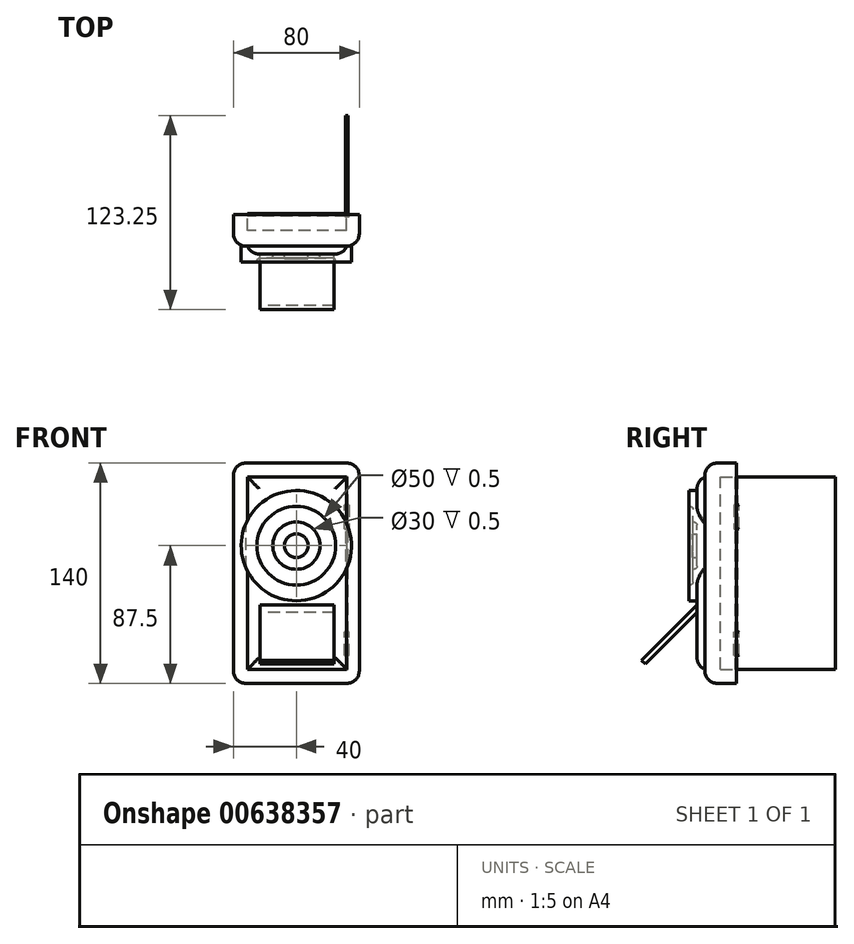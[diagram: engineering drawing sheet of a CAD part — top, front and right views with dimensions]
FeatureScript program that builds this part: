
annotation { "Feature Type Name" : "Feature", "Feature Type Description" : "" }
export const myFeature = defineFeature(function(context is Context, id is Id, definition is map)
    precondition{}
    {
        {
            var Q0;
            Q0=qCreatedBy(makeId("Front.planeOp"),FACE);
            var sketch = newSketch(context, id + "F0", { "sketchPlane" : qUnion([Q0])});
            skLineSegment(sketch, "E0", {"start": v(0, 0) * mm, "end": v(0, 140) * mm});
            skLineSegment(sketch, "E1", {"start": v(0, 140) * mm, "end": v(80, 140) * mm});
            skLineSegment(sketch, "E2", {"start": v(80, 140) * mm, "end": v(80, 0) * mm});
            skLineSegment(sketch, "E3", {"start": v(80, 0) * mm, "end": v(0, 0) * mm});
            skLineSegment(sketch, "E4", {"start": v(0, 0) * mm, "end": v(9, 0) * mm});
            skLineSegment(sketch, "E5", {"start": v(9, 0) * mm, "end": v(9, 131) * mm});
            skLineSegment(sketch, "E6", {"start": v(9, 131) * mm, "end": v(72, 131) * mm});
            skLineSegment(sketch, "E7", {"start": v(72, 131) * mm, "end": v(72, 9) * mm});
            skLineSegment(sketch, "E8", {"start": v(72, 9) * mm, "end": v(9, 9) * mm});
            skSolve(sketch);
        }
        {
            var Q0;
            Q0=makeQuery(id+"F0.imprint","IMPRINT",FACE,{"disambiguationData":[TD([[makeQuery(id+"F0.imprint","IMPRINT",EDGE,{"derivedFrom":sQuery(id+"F0.wireOp",EDGE,"E0")}),-1.0]])]});
            extrude(context, id + "F1", {"entities" : qUnion([Q0]), "depth" : 20 * mm, "offsetDistance" : 25 * mm});
        }
        {
            var Q0;
            {var subQ0=sQuery(id+"F0.wireOp",EDGE,"E6");Q0=makeQuery(id+"F0.imprint","IMPRINT",FACE,{"disambiguationData":[TD([[makeQuery(id+"F0.imprint","IMPRINT",EDGE,{"derivedFrom":subQ0}),-1.0]])]});}
            extrude(context, id + "F2", {"entities" : qUnion([Q0]), "operationType" : NewBodyOperationType.ADD, "depth" : 25 * mm, "offsetDistance" : 25 * mm});
        }
        {
            var Q0;
            {var subQ0=sQuery(id+"F0.wireOp",EDGE,"E6");Q0=makeQuery(id+"F0.imprint","IMPRINT",FACE,{"disambiguationData":[TD([[makeQuery(id+"F0.imprint","IMPRINT",EDGE,{"derivedFrom":subQ0}),-1.0]])]});}
            extrude(context, id + "F3", {"entities" : qUnion([Q0]), "operationType" : NewBodyOperationType.REMOVE, "depth" : 10 * mm, "offsetDistance" : 25 * mm});
        }
        {
            var Q0;
            Q0=makeQuery(id+"F1.opExtrude","SWEPT_EDGE",EDGE,{"disambiguationData":[OSD([sQuery(id+"F0.wireOp",EDGE,"E0"),sQuery(id+"F0.wireOp",EDGE,"E4")])]});
            var Q1;
            Q1=makeQuery(id+"F1.opExtrude","SWEPT_EDGE",EDGE,{"disambiguationData":[OSD([sQuery(id+"F0.wireOp",EDGE,"E2"),sQuery(id+"F0.wireOp",EDGE,"E3")])]});
            var Q2;
            Q2=makeQuery(id+"F1.opExtrude","SWEPT_EDGE",EDGE,{"disambiguationData":[OSD([sQuery(id+"F0.wireOp",EDGE,"E0"),sQuery(id+"F0.wireOp",EDGE,"E1")])]});
            var Q3;
            Q3=makeQuery(id+"F1.opExtrude","SWEPT_EDGE",EDGE,{"disambiguationData":[OSD([sQuery(id+"F0.wireOp",EDGE,"E1"),sQuery(id+"F0.wireOp",EDGE,"E2")])]});
            var Q4;
            Q4=makeQuery(id+"F1.opExtrude","CAP_EDGE",EDGE,{"disambiguationData":[OSD([sQuery(id+"F0.wireOp",EDGE,"E1")])],"isStart":false});
            var Q5;
            Q5=makeQuery(id+"F1.opExtrude","CAP_EDGE",EDGE,{"disambiguationData":[OSD([sQuery(id+"F0.wireOp",EDGE,"E0")])],"isStart":false});
            var Q6;
            Q6=makeQuery(id+"F1.opExtrude","CAP_EDGE",EDGE,{"disambiguationData":[OSD([sQuery(id+"F0.wireOp",EDGE,"E2")])],"isStart":false});
            var Q7;
            Q7=makeQuery(id+"F1.opExtrude","CAP_EDGE",EDGE,{"disambiguationData":[OSD([sQuery(id+"F0.wireOp",EDGE,"E3"),sQuery(id+"F0.wireOp",EDGE,"E4")])],"isStart":false});
            var Q8;
            Q8=makeQuery(id+"F2.opExtrude","CAP_EDGE",EDGE,{"disambiguationData":[OSD([sQuery(id+"F0.wireOp",EDGE,"E7")])],"isStart":false});
            var Q9;
            Q9=makeQuery(id+"F2.opExtrude","CAP_EDGE",EDGE,{"disambiguationData":[OSD([sQuery(id+"F0.wireOp",EDGE,"E6")])],"isStart":false});
            var Q10;
            Q10=makeQuery(id+"F2.opExtrude","CAP_EDGE",EDGE,{"disambiguationData":[OSD([sQuery(id+"F0.wireOp",EDGE,"E5")])],"isStart":false});
            var Q11;
            Q11=makeQuery(id+"F2.opExtrude","CAP_EDGE",EDGE,{"disambiguationData":[OSD([sQuery(id+"F0.wireOp",EDGE,"E8")])],"isStart":false});
            fillet(context, id + "F4", {"entities" : qUnion([Q0, Q1, Q2, Q3, Q4, Q5, Q6, Q7, Q8, Q9, Q10, Q11]), "radius" : 8 * mm, "tangentPropagation" : true, "allowEdgeOverflow" : false});
        }
        {
            var Q0;
            Q0=makeQuery(id+"F0.imprint","IMPRINT",FACE,{"disambiguationData":[TD([[makeQuery(id+"F0.imprint","IMPRINT",EDGE,{"derivedFrom":sQuery(id+"F0.wireOp",EDGE,"E0")}),-1.0]])]});
            var sketch = newSketch(context, id + "F5", { "sketchPlane" : qUnion([Q0])});
            skLineSegment(sketch, "E9", {"start": v(0, 0) * mm, "end": v(72, 0) * mm});
            skLineSegment(sketch, "E10", {"start": v(72, 0) * mm, "end": v(72, 131) * mm});
            skLineSegment(sketch, "E11", {"start": v(72, 131) * mm, "end": v(72, 65.5) * mm});
            skLineSegment(sketch, "E12", {"start": v(72, 65.5) * mm, "end": v(72, 98.25) * mm});
            skLineSegment(sketch, "E13", {"start": v(72, 98.25) * mm, "end": v(70.5, 98.25) * mm});
            skLineSegment(sketch, "E14", {"start": v(70.5, 98.25) * mm, "end": v(70.5, 113.25) * mm});
            skLineSegment(sketch, "E15", {"start": v(70.5, 113.25) * mm, "end": v(73.5, 113.25) * mm});
            skLineSegment(sketch, "E16", {"start": v(73.5, 113.25) * mm, "end": v(73.5, 98.25) * mm});
            skLineSegment(sketch, "E17", {"start": v(73.5, 98.25) * mm, "end": v(72, 98.25) * mm});
            skLineSegment(sketch, "E18.MirrorCS", {"start": v(73.5, 32.75) * mm, "end": v(72, 32.75) * mm});
            skLineSegment(sketch, "E19.MirrorCS", {"start": v(72, 32.75) * mm, "end": v(70.5, 32.75) * mm});
            skLineSegment(sketch, "E20.MirrorCS", {"start": v(70.5, 32.75) * mm, "end": v(70.5, 17.75) * mm});
            skLineSegment(sketch, "E21.MirrorCS", {"start": v(73.5, 17.75) * mm, "end": v(73.5, 32.75) * mm});
            skLineSegment(sketch, "E22.MirrorCS", {"start": v(70.5, 17.75) * mm, "end": v(73.5, 17.75) * mm});
            skSolve(sketch);
        }
        {
            var Q0;
            {var subQ4=sQuery(id+"F5.wireOp",EDGE,"E16");Q0=makeQuery(id+"F5.imprint","IMPRINT",FACE,{"disambiguationData":[TD([[makeQuery(id+"F5.imprint","IMPRINT",EDGE,{"derivedFrom":subQ4}),-1.0]])]});}
            var Q1;
            {var subQ0=sQuery(id+"F5.wireOp",EDGE,"E13");Q1=makeQuery(id+"F5.imprint","IMPRINT",FACE,{"disambiguationData":[TD([[makeQuery(id+"F5.imprint","IMPRINT",EDGE,{"derivedFrom":subQ0}),-1.0]])]});}
            var Q2;
            {var subQ0=sQuery(id+"F5.wireOp",EDGE,"E18.MirrorCS");Q2=makeQuery(id+"F5.imprint","IMPRINT",FACE,{"disambiguationData":[TD([[makeQuery(id+"F5.imprint","IMPRINT",EDGE,{"derivedFrom":subQ0}),1.0]])]});}
            var Q3;
            {var subQ0=sQuery(id+"F5.wireOp",EDGE,"E19.MirrorCS");Q3=makeQuery(id+"F5.imprint","IMPRINT",FACE,{"disambiguationData":[TD([[makeQuery(id+"F5.imprint","IMPRINT",EDGE,{"derivedFrom":subQ0}),1.0]])]});}
            extrude(context, id + "F6", {"entities" : qUnion([Q0, Q1, Q2, Q3]), "endBound" : BoundingType.SYMMETRIC, "depth" : 3 * mm, "offsetDistance" : 25 * mm});
        }
        {
            var Q0;
            Q0=makeQuery(id+"F6.opExtrude","CAP_EDGE",EDGE,{"disambiguationData":[OSD([sQuery(id+"F5.wireOp",EDGE,"E16")])],"isStart":true});
            var Q1;
            Q1=makeQuery(id+"F6.opExtrude","CAP_EDGE",EDGE,{"disambiguationData":[OSD([sQuery(id+"F5.wireOp",EDGE,"E14")])],"isStart":true});
            var Q2;
            Q2=makeQuery(id+"F6.opExtrude","CAP_EDGE",EDGE,{"disambiguationData":[OSD([sQuery(id+"F5.wireOp",EDGE,"E14")])],"isStart":false});
            var Q3;
            Q3=makeQuery(id+"F6.opExtrude","CAP_EDGE",EDGE,{"disambiguationData":[OSD([sQuery(id+"F5.wireOp",EDGE,"E21.MirrorCS")])],"isStart":true});
            var Q4;
            Q4=makeQuery(id+"F6.opExtrude","CAP_EDGE",EDGE,{"disambiguationData":[OSD([sQuery(id+"F5.wireOp",EDGE,"E20.MirrorCS")])],"isStart":true});
            var Q5;
            Q5=makeQuery(id+"F6.opExtrude","CAP_EDGE",EDGE,{"disambiguationData":[OSD([sQuery(id+"F5.wireOp",EDGE,"E20.MirrorCS")])],"isStart":false});
            fillet(context, id + "F7", {"entities" : qUnion([Q0, Q1, Q2, Q3, Q4, Q5]), "radius" : 1.5 * mm, "tangentPropagation" : true, "allowEdgeOverflow" : false});
        }
        {
            var Q0;
            Q0=qCreatedBy(makeId("Front.planeOp"),FACE);
            var sketch = newSketch(context, id + "F8", { "sketchPlane" : qUnion([Q0])});
            skLineSegment(sketch, "E23", {"start": v(0, 0) * mm, "end": v(72, 0) * mm});
            skLineSegment(sketch, "E24", {"start": v(72, 0) * mm, "end": v(72, 9) * mm});
            skLineSegment(sketch, "E25", {"start": v(72, 9) * mm, "end": v(72, 131) * mm});
            skLineSegment(sketch, "E26", {"start": v(72, 131) * mm, "end": v(72.75, 131) * mm});
            skLineSegment(sketch, "E27", {"start": v(72.75, 131) * mm, "end": v(72, 131) * mm});
            skLineSegment(sketch, "E28", {"start": v(72, 131) * mm, "end": v(71.25, 131) * mm});
            skLineSegment(sketch, "E29", {"start": v(71.25, 131) * mm, "end": v(71.25, 9) * mm});
            skLineSegment(sketch, "E30", {"start": v(71.25, 9) * mm, "end": v(72.75, 9) * mm});
            skLineSegment(sketch, "E31", {"start": v(72.75, 9) * mm, "end": v(72.75, 131) * mm});
            skSolve(sketch);
        }
        {
            var Q0;
            {var subQ0=sQuery(id+"F8.wireOp",EDGE,"E25");Q0=makeQuery(id+"F8.imprint","IMPRINT",FACE,{"disambiguationData":[TD([[makeQuery(id+"F8.imprint","IMPRINT",EDGE,{"derivedFrom":subQ0}),1.0]])]});}
            var Q1;
            {var subQ0=sQuery(id+"F8.wireOp",EDGE,"E25");Q1=makeQuery(id+"F8.imprint","IMPRINT",FACE,{"disambiguationData":[TD([[makeQuery(id+"F8.imprint","IMPRINT",EDGE,{"derivedFrom":subQ0}),-1.0]])]});}
            extrude(context, id + "F9", {"entities" : qUnion([Q0, Q1]), "oppositeDirection" : true, "depth" : 63 * mm, "offsetDistance" : 25 * mm});
        }
        {
            var Q0;
            Q0=qCreatedBy(makeId("Front.planeOp"),FACE);
            var sketch = newSketch(context, id + "F10", { "sketchPlane" : qUnion([Q0])});
            skLineSegment(sketch, "E32", {"start": v(0, 0) * mm, "end": v(72, 0) * mm});
            skLineSegment(sketch, "E33", {"start": v(72, 0) * mm, "end": v(72, 9) * mm});
            skLineSegment(sketch, "E34", {"start": v(72, 9) * mm, "end": v(9, 9) * mm});
            skLineSegment(sketch, "E35", {"start": v(9, 9) * mm, "end": v(9, 131) * mm});
            skLineSegment(sketch, "E36", {"start": v(9, 131) * mm, "end": v(72, 131) * mm});
            skLineSegment(sketch, "E37", {"start": v(72, 131) * mm, "end": v(72, 9) * mm});
            skSolve(sketch);
        }
        {
            var Q0;
            Q0=makeQuery(id+"F10.imprint","IMPRINT",FACE,{"disambiguationData":[TD([[makeQuery(id+"F10.imprint","IMPRINT",EDGE,{"derivedFrom":sQuery(id+"F10.wireOp",EDGE,"E34")}),-1.0]])]});
            extrude(context, id + "F11", {"entities" : qUnion([Q0]), "endBound" : BoundingType.SYMMETRIC, "depth" : 1.5 * mm, "offsetDistance" : 25 * mm});
        }
        {
            var Q0;
            Q0=qCreatedBy(makeId("Right.planeOp"),FACE);
            var sketch = newSketch(context, id + "F12", { "sketchPlane" : qUnion([Q0])});
            skLineSegment(sketch, "E38", {"start": v(0, 0) * mm, "end": v(-25, 0) * mm});
            skLineSegment(sketch, "E39", {"start": v(-25, 0) * mm, "end": v(-25, 50) * mm});
            skLineSegment(sketch, "E40", {"start": v(-50, 25) * mm, "end": v(-60.25, 14.75) * mm});
            skLineSegment(sketch, "E41", {"start": v(-50, 25) * mm, "end": v(-25, 50) * mm});
            skLineSegment(sketch, "E42", {"start": v(-60.25, 14.75) * mm, "end": v(-57.78, 12.27) * mm});
            skLineSegment(sketch, "E43", {"start": v(-57.78, 12.27) * mm, "end": v(-25, 45.05) * mm});
            skLineSegment(sketch, "E44", {"start": v(-25, 45.05) * mm, "end": v(-25, 50) * mm});
            skSolve(sketch);
        }
        {
            var Q0;
            Q0=makeQuery(id+"F12.imprint","IMPRINT",FACE,{"disambiguationData":[TD([[makeQuery(id+"F12.imprint","IMPRINT",EDGE,{"derivedFrom":sQuery(id+"F12.wireOp",EDGE,"E40")}),1.0]])]});
            extrude(context, id + "F13", {"entities" : qUnion([Q0]), "operationType" : NewBodyOperationType.ADD, "depth" : 64 * mm, "offsetDistance" : 25 * mm});
        }
        {
            var Q0;
            Q0=makeQuery(id+"F13.opExtrude","CAP_FACE",FACE,{"disambiguationData":[OSD([sQuery(id+"F12.wireOp",EDGE,"E39"),sQuery(id+"F12.wireOp",EDGE,"E40"),sQuery(id+"F12.wireOp",EDGE,"E41"),sQuery(id+"F12.wireOp",EDGE,"E42"),sQuery(id+"F12.wireOp",EDGE,"E43")])],"isStart":true});
            extrude(context, id + "F14", {"entities" : qUnion([Q0]), "operationType" : NewBodyOperationType.REMOVE, "oppositeDirection" : true, "depth" : 17 * mm, "offsetDistance" : 25 * mm});
        }
        {
            var Q0;
            Q0=makeQuery(id+"F14.boolean.opBoolean","MERGE",FACE,{"derivedFrom":[makeQuery(id+"F2.opExtrude","CAP_FACE",FACE,{"disambiguationData":[OSD([sQuery(id+"F0.wireOp",EDGE,"E5"),sQuery(id+"F0.wireOp",EDGE,"E6"),sQuery(id+"F0.wireOp",EDGE,"E7"),sQuery(id+"F0.wireOp",EDGE,"E8")])],"isStart":false})],"fromTools":[makeQuery(id+"F14.opExtrude","SWEPT_FACE",FACE,{"disambiguationData":[OSD([sQuery(id+"F12.wireOp",EDGE,"E39")])]})]});
            var sketch = newSketch(context, id + "F15", { "sketchPlane" : qUnion([Q0])});
            skLineSegment(sketch, "E45", {"start": v(0, 0) * mm, "end": v(40, 0) * mm});
            skLineSegment(sketch, "E46", {"start": v(40, 0) * mm, "end": v(40, 140) * mm});
            skLineSegment(sketch, "E47", {"start": v(40, 140) * mm, "end": v(40, 70) * mm});
            skLineSegment(sketch, "E48", {"start": v(40, 70) * mm, "end": v(40, 105) * mm});
            skLineSegment(sketch, "E49", {"start": v(40, 105) * mm, "end": v(40, 87.5) * mm});
            skCircle(sketch, "E50", {"center": v(40, 87.5) * mm, "radius": 35 * mm});
            skSolve(sketch);
        }
        {
            var Q0;
            {var subQ0=sQuery(id+"F15.wireOp",EDGE,"E50");var subQ1=sQuery(id+"F0.wireOp",EDGE,"E7");var subQ2=makeQuery(id+"F4.opFillet","BLEND_EDGE",EDGE,{"blendedFrom":[makeQuery(id+"F2.opExtrude","CAP_EDGE",EDGE,{"disambiguationData":[OSD([subQ1])],"isStart":false}),makeQuery(id+"F2.opExtrude","CAP_FACE",FACE,{"disambiguationData":[OSD([sQuery(id+"F0.wireOp",EDGE,"E5"),sQuery(id+"F0.wireOp",EDGE,"E6"),subQ1,sQuery(id+"F0.wireOp",EDGE,"E8")])],"isStart":false})],"blendedInto":[makeQuery(id+"F2.opExtrude","CAP_FACE",FACE,{"disambiguationData":[OSD([sQuery(id+"F0.wireOp",EDGE,"E5"),sQuery(id+"F0.wireOp",EDGE,"E6"),subQ1,sQuery(id+"F0.wireOp",EDGE,"E8")])],"isStart":false})]});var subQ3=makeQuery(id+"F15.imprint","INTERSECT",VERTEX,{"disambiguationData":[OD(0.0)],"derivedFrom":[subQ2,subQ0]});Q0=makeQuery(id+"F15.imprint","IMPRINT",FACE,{"disambiguationData":[TD([[makeQuery(id+"F15.imprint","IMPRINT",EDGE,{"disambiguationData":[TD([[subQ3,-1.0]])],"derivedFrom":subQ0}),1.0]])]});}
            var Q1;
            {var subQ0=sQuery(id+"F15.wireOp",EDGE,"E46");var subQ5=makeQuery(id+"F15.imprint","IMPRINT",VERTEX,{"disambiguationData":[OD(1.0)],"derivedFrom":subQ0});Q1=makeQuery(id+"F15.imprint","IMPRINT",FACE,{"disambiguationData":[TD([[makeQuery(id+"F15.imprint","IMPRINT",EDGE,{"disambiguationData":[TD([[subQ5,-1.0]])],"derivedFrom":subQ0}),-1.0]])]});}
            var Q2;
            {var subQ0=sQuery(id+"F15.wireOp",EDGE,"E46");var subQ5=makeQuery(id+"F15.imprint","IMPRINT",VERTEX,{"disambiguationData":[OD(1.0)],"derivedFrom":subQ0});Q2=makeQuery(id+"F15.imprint","IMPRINT",FACE,{"disambiguationData":[TD([[makeQuery(id+"F15.imprint","IMPRINT",EDGE,{"disambiguationData":[TD([[subQ5,-1.0]])],"derivedFrom":subQ0}),1.0]])]});}
            var Q3;
            {var subQ0=sQuery(id+"F15.wireOp",EDGE,"E50");var subQ1=sQuery(id+"F0.wireOp",EDGE,"E5");var subQ2=makeQuery(id+"F4.opFillet","BLEND_FACE",FACE,{"disambiguationData":[OSD([subQ1])]});var subQ3=makeQuery(id+"F13.opExtrude","SWEPT_FACE",FACE,{"disambiguationData":[OSD([sQuery(id+"F12.wireOp",EDGE,"E39")])]});var subQ4=sQuery(id+"F0.wireOp",EDGE,"E8");var subQ5=sQuery(id+"F0.wireOp",EDGE,"E6");var subQ6=makeQuery(id+"F2.opExtrude","CAP_FACE",FACE,{"disambiguationData":[OSD([subQ1,subQ5,sQuery(id+"F0.wireOp",EDGE,"E7"),subQ4])],"isStart":false});var subQ7=makeQuery(id+"F4.opFillet","BLEND_EDGE",EDGE,{"blendedFrom":[makeQuery(id+"F2.opExtrude","CAP_EDGE",EDGE,{"disambiguationData":[OSD([subQ1])],"isStart":false}),subQ6],"blendedInto":[subQ6]});var subQ8=makeQuery(id+"F14.boolean.opBoolean","MERGE",EDGE,{"derivedFrom":[makeQuery(id+"F13.boolean.opBoolean","SPLIT",EDGE,{"disambiguationData":[topologyDisambiguationEdgeConnected([subQ6,subQ2]),TD([makeQuery(id+"F4.opFillet","BLEND_FACE",FACE,{"disambiguationData":[OSD([subQ5])]})])],"derivedFrom":subQ7}),makeQuery(id+"F13.boolean.opBoolean","SPLIT",EDGE,{"disambiguationData":[topologyDisambiguationEdgeConnected([subQ6,subQ2]),TD([makeQuery(id+"F4.opFillet","BLEND_FACE",FACE,{"disambiguationData":[OSD([subQ4])]})])],"derivedFrom":subQ7}),makeQuery(id+"F13.boolean.opBoolean","SPLIT",EDGE,{"disambiguationData":[topologyDisambiguationEdgeConnected([subQ2,subQ3])],"derivedFrom":subQ7})]});var subQ9=makeQuery(id+"F15.imprint","INTERSECT",VERTEX,{"disambiguationData":[OD(0.0)],"derivedFrom":[subQ8,subQ0]});Q3=makeQuery(id+"F15.imprint","IMPRINT",FACE,{"disambiguationData":[TD([[makeQuery(id+"F15.imprint","IMPRINT",EDGE,{"disambiguationData":[TD([[subQ9,-1.0]])],"derivedFrom":subQ0}),1.0]])]});}
            extrude(context, id + "F16", {"entities" : qUnion([Q0, Q1, Q2, Q3]), "operationType" : NewBodyOperationType.ADD, "endBound" : BoundingType.SYMMETRIC, "depth" : 10 * mm, "offsetDistance" : 25 * mm});
        }
        {
            var Q0;
            Q0=makeQuery(id+"F16.opExtrude","CAP_FACE",FACE,{"disambiguationData":[OSD([sQuery(id+"F15.wireOp",EDGE,"E50")])],"isStart":false});
            var sketch = newSketch(context, id + "F17", { "sketchPlane" : qUnion([Q0])});
            skCircle(sketch, "E51", {"center": v(40, 87.5) * mm, "radius": 25 * mm});
            skSolve(sketch);
        }
        {
            var Q0;
            Q0=makeQuery(id+"F17.imprint","IMPRINT",FACE,{"disambiguationData":[TD([[makeQuery(id+"F17.imprint","IMPRINT",EDGE,{"derivedFrom":sQuery(id+"F17.wireOp",EDGE,"E51")}),1.0]])]});
            extrude(context, id + "F18", {"entities" : qUnion([Q0]), "operationType" : NewBodyOperationType.REMOVE, "oppositeDirection" : true, "depth" : 2.5 * mm, "offsetDistance" : 25 * mm});
        }
        {
            var Q0;
            Q0=makeQuery(id+"F18.boolean.opBoolean","COPY",FACE,{"derivedFrom":makeQuery(id+"F18.opExtrude","CAP_FACE",FACE,{"disambiguationData":[OSD([sQuery(id+"F17.wireOp",EDGE,"E51")])],"isStart":false})});
            var sketch = newSketch(context, id + "F19", { "sketchPlane" : qUnion([Q0])});
            skCircle(sketch, "E52", {"center": v(40, 87.5) * mm, "radius": 15 * mm});
            skSolve(sketch);
        }
        {
            var Q0;
            Q0=makeQuery(id+"F19.imprint","IMPRINT",FACE,{"disambiguationData":[TD([[makeQuery(id+"F19.imprint","IMPRINT",EDGE,{"derivedFrom":sQuery(id+"F19.wireOp",EDGE,"E52")}),1.0]])]});
            extrude(context, id + "F20", {"entities" : qUnion([Q0]), "operationType" : NewBodyOperationType.REMOVE, "oppositeDirection" : true, "depth" : 2.5 * mm, "offsetDistance" : 25 * mm});
        }
        {
            var Q0;
            Q0=makeQuery(id+"F20.boolean.opBoolean","COPY",FACE,{"derivedFrom":makeQuery(id+"F20.opExtrude","CAP_FACE",FACE,{"disambiguationData":[OSD([sQuery(id+"F19.wireOp",EDGE,"E52")])],"isStart":false})});
            var sketch = newSketch(context, id + "F21", { "sketchPlane" : qUnion([Q0])});
            skCircle(sketch, "E53", {"center": v(40, 87.5) * mm, "radius": 7.5 * mm});
            skSolve(sketch);
        }
        {
            var Q0;
            Q0=makeQuery(id+"F21.imprint","IMPRINT",FACE,{"disambiguationData":[TD([[makeQuery(id+"F21.imprint","IMPRINT",EDGE,{"derivedFrom":sQuery(id+"F21.wireOp",EDGE,"E53")}),1.0]])]});
            extrude(context, id + "F22", {"entities" : qUnion([Q0]), "operationType" : NewBodyOperationType.ADD, "depth" : 3 * mm, "offsetDistance" : 25 * mm});
        }
        {
            var Q0;
            Q0=makeQuery(id+"F18.boolean.opBoolean","COPY",EDGE,{"derivedFrom":makeQuery(id+"F18.opExtrude","CAP_EDGE",EDGE,{"disambiguationData":[OSD([sQuery(id+"F17.wireOp",EDGE,"E51")])],"isStart":false})});
            var Q1;
            Q1=makeQuery(id+"F20.boolean.opBoolean","COPY",EDGE,{"derivedFrom":makeQuery(id+"F20.opExtrude","CAP_EDGE",EDGE,{"disambiguationData":[OSD([sQuery(id+"F19.wireOp",EDGE,"E52")])],"isStart":false})});
            var Q2;
            Q2=makeQuery(id+"F22.opExtrude","CAP_EDGE",EDGE,{"disambiguationData":[OSD([sQuery(id+"F21.wireOp",EDGE,"E53")])],"isStart":true});
            fillet(context, id + "F23", {"entities" : qUnion([Q0, Q1, Q2]), "radius" : 2 * mm, "tangentPropagation" : true, "allowEdgeOverflow" : false});
        }
    });
